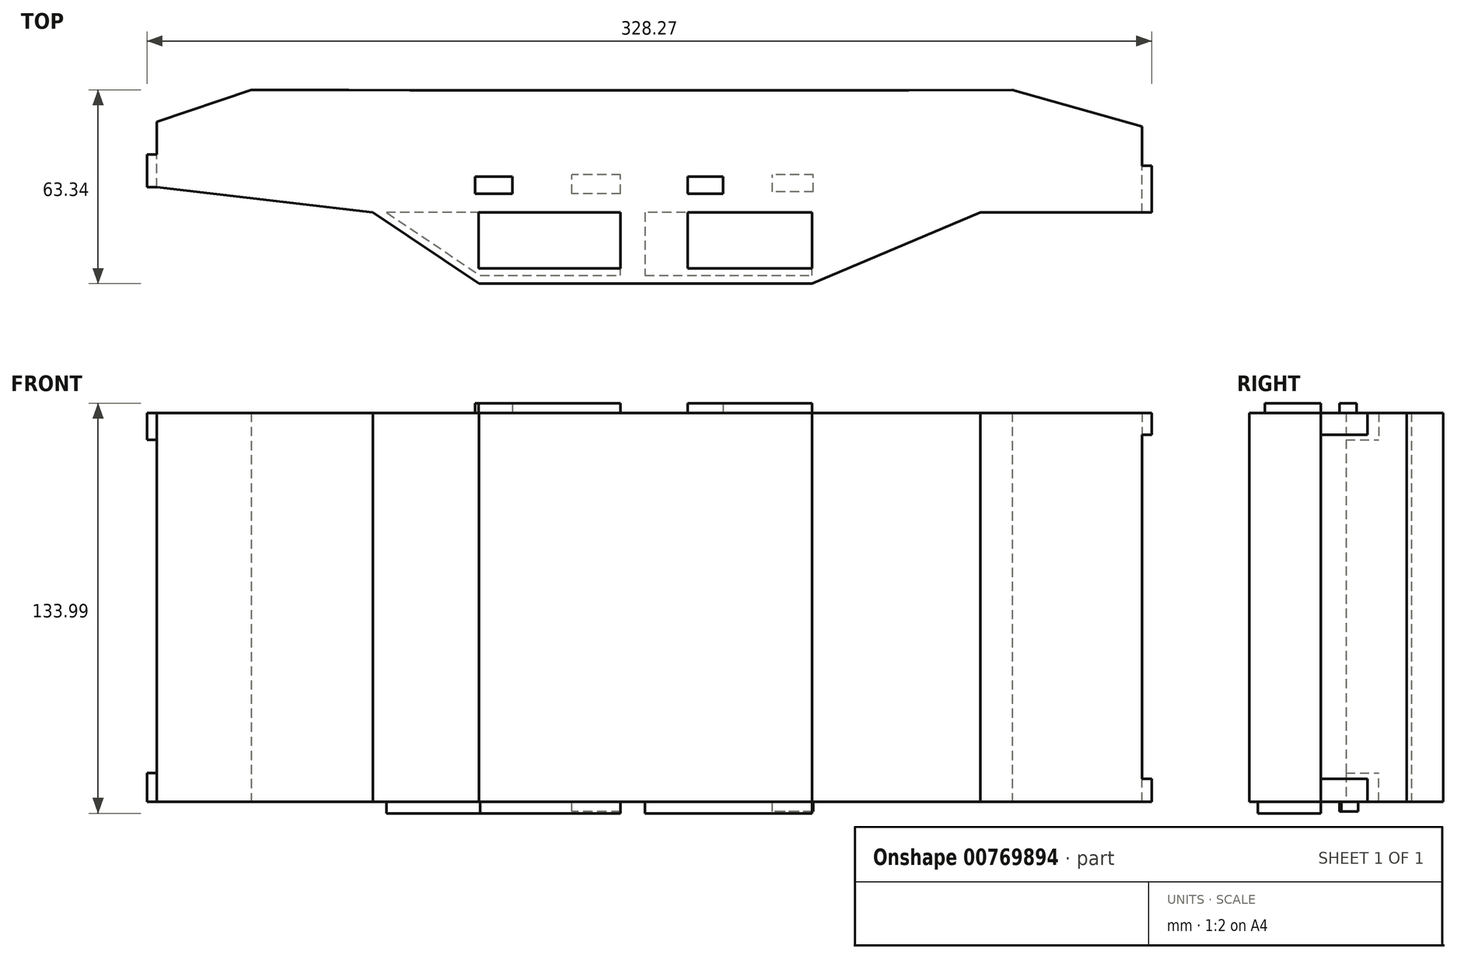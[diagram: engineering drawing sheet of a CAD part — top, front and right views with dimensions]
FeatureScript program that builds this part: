
annotation { "Feature Type Name" : "Feature", "Feature Type Description" : "" }
export const myFeature = defineFeature(function(context is Context, id is Id, definition is map)
    precondition{}
    {
        {
            var Q0;
            Q0=qCreatedBy(makeId("Top.planeOp"),FACE);
            var sketch = newSketch(context, id + "F0", { "sketchPlane" : qUnion([Q0])});
            skCircle(sketch, "E0", {"center": v(-68.64, 11.59) * mm, "radius": 18.95 * mm});
            skCircle(sketch, "E1", {"center": v(94.23, 11.59) * mm, "radius": 18.94 * mm});
            skLineSegment(sketch, "E2", {"start": v(-46.32, -70.57) * mm, "end": v(62.61, -70.57) * mm});
            skLineSegment(sketch, "E3", {"start": v(-46.32, -70.57) * mm, "end": v(-80.9, -47.31) * mm});
            skLineSegment(sketch, "E4", {"start": v(-80.9, -47.31) * mm, "end": v(-151.57, -39.05) * mm});
            skLineSegment(sketch, "E5", {"start": v(-151.57, -39.05) * mm, "end": v(-151.57, -17.64) * mm});
            skLineSegment(sketch, "E6", {"start": v(-151.57, -17.64) * mm, "end": v(-120.73, -7.23) * mm});
            skLineSegment(sketch, "E7", {"start": v(-120.73, -7.23) * mm, "end": v(-88.85, -7.23) * mm});
            skLineSegment(sketch, "E8", {"start": v(-46.32, -7.23) * mm, "end": v(62.61, -7.23) * mm});
            skLineSegment(sketch, "E9", {"start": v(62.61, -70.57) * mm, "end": v(117.59, -47.31) * mm});
            skLineSegment(sketch, "E10", {"start": v(117.59, -47.31) * mm, "end": v(170.34, -47.31) * mm});
            skLineSegment(sketch, "E11", {"start": v(170.34, -47.31) * mm, "end": v(170.34, -19.22) * mm});
            skLineSegment(sketch, "E12", {"start": v(170.34, -19.22) * mm, "end": v(127.98, -7.23) * mm});
            skLineSegment(sketch, "E13", {"start": v(-68.64, 11.59) * mm, "end": v(94.23, 11.59) * mm});
            skLineSegment(sketch, "E14", {"start": v(-68.64, -7.36) * mm, "end": v(94.23, -7.36) * mm});
            skLineSegment(sketch, "E15", {"start": v(-88.85, -7.23) * mm, "end": v(-68.64, -7.36) * mm});
            skLineSegment(sketch, "E16", {"start": v(127.98, -7.23) * mm, "end": v(94.23, -7.36) * mm});
            skSolve(sketch);
        }
        {
            var Q0;
            Q0=sQuery(id+"F0.wireOp",EDGE,"E0");
            var Q1;
            Q1=sQuery(id+"F0.wireOp",EDGE,"E1");
            extrude(context, id + "F1", {"bodyType" : ToolBodyType.SURFACE, "surfaceEntities" : qUnion([Q0, Q1]), "endBound" : BoundingType.SYMMETRIC, "depth" : 25.4 * mm, "offsetDistance" : 25.4 * mm});
        }
        {
            var Q0;
            Q0=qCreatedBy(makeId("Top.planeOp"),FACE);
            cPlane(context, id + "F2", {"entities" : qUnion([Q0]), "cplaneType" : CPlaneType.OFFSET, "offset" : 127 * mm, "width" : 152.4 * mm, "height" : 152.4 * mm});
        }
        {
            var Q0;
            Q0=qCreatedBy(id+"F2.planeOp",FACE);
            var sketch = newSketch(context, id + "F3", { "sketchPlane" : qUnion([Q0])});
            skCircle(sketch, "E17", {"center": v(-69.62, 11.2) * mm, "radius": 18.95 * mm});
            skCircle(sketch, "E18", {"center": v(95.63, 11.75) * mm, "radius": 18.95 * mm});
            skSolve(sketch);
        }
        {
            var Q0;
            Q0=sQuery(id+"F3.wireOp",EDGE,"E18");
            var Q1;
            Q1=sQuery(id+"F3.wireOp",EDGE,"E17");
            extrude(context, id + "F4", {"bodyType" : ToolBodyType.SURFACE, "surfaceEntities" : qUnion([Q0, Q1]), "endBound" : BoundingType.SYMMETRIC, "depth" : 25.4 * mm, "offsetDistance" : 25.4 * mm});
        }
        {
            var Q0;
            Q0=makeQuery(id+"F0.imprint","IMPRINT",FACE,{"disambiguationData":[TD([[makeQuery(id+"F0.imprint","IMPRINT",EDGE,{"derivedFrom":sQuery(id+"F0.wireOp",EDGE,"E2")}),1.0]])]});
            extrude(context, id + "F5", {"entities" : qUnion([Q0]), "depth" : 127 * mm, "offsetDistance" : 25.4 * mm});
        }
        {
            var Q0;
            Q0=makeQuery(id+"F5.opExtrude","CAP_FACE",FACE,{"disambiguationData":[OSD([sQuery(id+"F0.wireOp",EDGE,"E0"),sQuery(id+"F0.wireOp",EDGE,"E2"),sQuery(id+"F0.wireOp",EDGE,"E3"),sQuery(id+"F0.wireOp",EDGE,"E4"),sQuery(id+"F0.wireOp",EDGE,"E5"),sQuery(id+"F0.wireOp",EDGE,"E6"),sQuery(id+"F0.wireOp",EDGE,"E7"),sQuery(id+"F0.wireOp",EDGE,"E9"),sQuery(id+"F0.wireOp",EDGE,"E10"),sQuery(id+"F0.wireOp",EDGE,"E11"),sQuery(id+"F0.wireOp",EDGE,"E12"),sQuery(id+"F0.wireOp",EDGE,"E14"),sQuery(id+"F0.wireOp",EDGE,"E15"),sQuery(id+"F0.wireOp",EDGE,"E16")])],"isStart":true});
            var sketch = newSketch(context, id + "F6", { "sketchPlane" : qUnion([Q0])});
            skLineSegment(sketch, "E19", {"start": v(-76.42, 47.31) * mm, "end": v(-45.87, 67.86) * mm});
            skLineSegment(sketch, "E20", {"start": v(-45.87, 67.86) * mm, "end": v(0, 67.86) * mm});
            skLineSegment(sketch, "E21", {"start": v(0, 67.86) * mm, "end": v(0, 47.31) * mm});
            skLineSegment(sketch, "E22", {"start": v(0, 47.31) * mm, "end": v(-76.42, 47.31) * mm});
            skLineSegment(sketch, "E23", {"start": v(8.01, 67.86) * mm, "end": v(62.61, 67.86) * mm});
            skLineSegment(sketch, "E24", {"start": v(62.61, 67.86) * mm, "end": v(62.61, 47.31) * mm});
            skLineSegment(sketch, "E25", {"start": v(62.61, 47.31) * mm, "end": v(8.01, 47.31) * mm});
            skLineSegment(sketch, "E26", {"start": v(8.01, 47.31) * mm, "end": v(8.01, 67.86) * mm});
            skSolve(sketch);
        }
        {
            var Q0;
            Q0=makeQuery(id+"F6.imprint","IMPRINT",FACE,{"disambiguationData":[TD([[makeQuery(id+"F6.imprint","IMPRINT",EDGE,{"derivedFrom":sQuery(id+"F6.wireOp",EDGE,"E19")}),-1.0]])]});
            var Q1;
            Q1=makeQuery(id+"F6.imprint","IMPRINT",FACE,{"disambiguationData":[TD([[makeQuery(id+"F6.imprint","IMPRINT",EDGE,{"derivedFrom":sQuery(id+"F6.wireOp",EDGE,"E23")}),-1.0]])]});
            extrude(context, id + "F7", {"entities" : qUnion([Q0, Q1]), "operationType" : NewBodyOperationType.ADD, "depth" : 3.8 * mm, "offsetDistance" : 25.4 * mm});
        }
        {
            var Q0;
            Q0=makeQuery(id+"F5.opExtrude","SWEPT_FACE",FACE,{"disambiguationData":[OSD([sQuery(id+"F0.wireOp",EDGE,"E11")])]});
            var sketch = newSketch(context, id + "F8", { "sketchPlane" : qUnion([Q0])});
            skLineSegment(sketch, "E27.bottom", {"start": v(-47.31, 0) * mm, "end": v(-31.96, 0) * mm});
            skLineSegment(sketch, "E27.top", {"start": v(-47.31, 7.4) * mm, "end": v(-31.96, 7.4) * mm});
            skLineSegment(sketch, "E27.left", {"start": v(-47.31, 0) * mm, "end": v(-47.31, 7.4) * mm});
            skLineSegment(sketch, "E27.right", {"start": v(-31.96, 0) * mm, "end": v(-31.96, 7.4) * mm});
            skLineSegment(sketch, "E28.bottom", {"start": v(-47.31, 127) * mm, "end": v(-31.96, 127) * mm});
            skLineSegment(sketch, "E28.top", {"start": v(-47.31, 119.88) * mm, "end": v(-31.96, 119.88) * mm});
            skLineSegment(sketch, "E28.left", {"start": v(-47.31, 127) * mm, "end": v(-47.31, 119.88) * mm});
            skLineSegment(sketch, "E28.right", {"start": v(-31.96, 127) * mm, "end": v(-31.96, 119.88) * mm});
            skSolve(sketch);
        }
        {
            var Q0;
            Q0 = qSketchRegion(id + "F8", true);
            extrude(context, id + "F9", {"entities" : qUnion([Q0]), "operationType" : NewBodyOperationType.ADD, "depth" : 3.17 * mm, "offsetDistance" : 25.4 * mm});
        }
        {
            var Q0;
            Q0=makeQuery(id+"F5.opExtrude","SWEPT_FACE",FACE,{"disambiguationData":[OSD([sQuery(id+"F0.wireOp",EDGE,"E5")])]});
            var sketch = newSketch(context, id + "F10", { "sketchPlane" : qUnion([Q0])});
            skPoint(sketch, "E29.oppositeSnap0", {"position": v(28.35, 127) * mm});
            skLineSegment(sketch, "E29.bottom", {"start": v(39.05, 127) * mm, "end": v(28.35, 127) * mm});
            skLineSegment(sketch, "E29.top", {"start": v(39.05, 118.22) * mm, "end": v(28.35, 118.22) * mm});
            skLineSegment(sketch, "E29.left", {"start": v(39.05, 127) * mm, "end": v(39.05, 118.22) * mm});
            skLineSegment(sketch, "E29.right", {"start": v(28.35, 127) * mm, "end": v(28.35, 118.22) * mm});
            skLineSegment(sketch, "E30.bottom", {"start": v(39.05, 0) * mm, "end": v(28.35, 0) * mm});
            skLineSegment(sketch, "E30.top", {"start": v(39.05, 9.33) * mm, "end": v(28.35, 9.33) * mm});
            skLineSegment(sketch, "E30.left", {"start": v(39.05, 0) * mm, "end": v(39.05, 9.33) * mm});
            skLineSegment(sketch, "E30.right", {"start": v(28.35, 0) * mm, "end": v(28.35, 9.33) * mm});
            skSolve(sketch);
        }
        {
            var Q0;
            Q0=makeQuery(id+"F10.imprint","IMPRINT",FACE,{"disambiguationData":[TD([[makeQuery(id+"F10.imprint","IMPRINT",EDGE,{"derivedFrom":sQuery(id+"F10.wireOp",EDGE,"E29.bottom")}),1.0]])]});
            var Q1;
            Q1=makeQuery(id+"F10.imprint","IMPRINT",FACE,{"disambiguationData":[TD([[makeQuery(id+"F10.imprint","IMPRINT",EDGE,{"derivedFrom":sQuery(id+"F10.wireOp",EDGE,"E30.bottom")}),-1.0]])]});
            extrude(context, id + "F11", {"entities" : qUnion([Q0, Q1]), "operationType" : NewBodyOperationType.ADD, "depth" : 3.17 * mm, "offsetDistance" : 25.4 * mm});
        }
        {
            var Q0;
            Q0=makeQuery(id+"F11.boolean.opBoolean","MERGE",FACE,{"derivedFrom":[makeQuery(id+"F9.boolean.opBoolean","MERGE",FACE,{"derivedFrom":[makeQuery(id+"F5.opExtrude","CAP_FACE",FACE,{"disambiguationData":[OSD([sQuery(id+"F0.wireOp",EDGE,"E0"),sQuery(id+"F0.wireOp",EDGE,"E2"),sQuery(id+"F0.wireOp",EDGE,"E3"),sQuery(id+"F0.wireOp",EDGE,"E4"),sQuery(id+"F0.wireOp",EDGE,"E5"),sQuery(id+"F0.wireOp",EDGE,"E6"),sQuery(id+"F0.wireOp",EDGE,"E7"),sQuery(id+"F0.wireOp",EDGE,"E9"),sQuery(id+"F0.wireOp",EDGE,"E10"),sQuery(id+"F0.wireOp",EDGE,"E11"),sQuery(id+"F0.wireOp",EDGE,"E12"),sQuery(id+"F0.wireOp",EDGE,"E14"),sQuery(id+"F0.wireOp",EDGE,"E15"),sQuery(id+"F0.wireOp",EDGE,"E16")])],"isStart":false}),makeQuery(id+"F9.opExtrude","SWEPT_FACE",FACE,{"disambiguationData":[OSD([sQuery(id+"F8.wireOp",EDGE,"E28.bottom")])]})]}),makeQuery(id+"F11.opExtrude","SWEPT_FACE",FACE,{"disambiguationData":[OSD([sQuery(id+"F10.wireOp",EDGE,"E29.bottom")])]})]});
            var sketch = newSketch(context, id + "F12", { "sketchPlane" : qUnion([Q0])});
            skLineSegment(sketch, "E31", {"start": v(62.61, -65.57) * mm, "end": v(21.89, -65.57) * mm});
            skLineSegment(sketch, "E32", {"start": v(21.89, -65.57) * mm, "end": v(21.89, -47.31) * mm});
            skLineSegment(sketch, "E33", {"start": v(21.89, -47.31) * mm, "end": v(62.61, -47.31) * mm});
            skLineSegment(sketch, "E34", {"start": v(62.61, -47.31) * mm, "end": v(62.61, -65.57) * mm});
            skLineSegment(sketch, "E35", {"start": v(-46.45, -65.57) * mm, "end": v(-46.45, -47.31) * mm});
            skLineSegment(sketch, "E36", {"start": v(-46.45, -47.31) * mm, "end": v(0, -47.31) * mm});
            skLineSegment(sketch, "E37", {"start": v(0, -47.31) * mm, "end": v(0, -65.57) * mm});
            skLineSegment(sketch, "E38", {"start": v(0, -65.57) * mm, "end": v(-46.45, -65.57) * mm});
            skSolve(sketch);
        }
        {
            var Q0;
            Q0=makeQuery(id+"F12.imprint","IMPRINT",FACE,{"disambiguationData":[TD([[makeQuery(id+"F12.imprint","IMPRINT",EDGE,{"derivedFrom":sQuery(id+"F12.wireOp",EDGE,"E31")}),-1.0]])]});
            var Q1;
            Q1=makeQuery(id+"F12.imprint","IMPRINT",FACE,{"disambiguationData":[TD([[makeQuery(id+"F12.imprint","IMPRINT",EDGE,{"derivedFrom":sQuery(id+"F12.wireOp",EDGE,"E35")}),-1.0]])]});
            extrude(context, id + "F13", {"entities" : qUnion([Q0, Q1]), "operationType" : NewBodyOperationType.ADD, "depth" : 3.17 * mm, "offsetDistance" : 25.4 * mm});
        }
        {
            var Q0;
            Q0=makeQuery(id+"F11.boolean.opBoolean","MERGE",FACE,{"derivedFrom":[makeQuery(id+"F9.boolean.opBoolean","MERGE",FACE,{"derivedFrom":[makeQuery(id+"F5.opExtrude","CAP_FACE",FACE,{"disambiguationData":[OSD([sQuery(id+"F0.wireOp",EDGE,"E0"),sQuery(id+"F0.wireOp",EDGE,"E2"),sQuery(id+"F0.wireOp",EDGE,"E3"),sQuery(id+"F0.wireOp",EDGE,"E4"),sQuery(id+"F0.wireOp",EDGE,"E5"),sQuery(id+"F0.wireOp",EDGE,"E6"),sQuery(id+"F0.wireOp",EDGE,"E7"),sQuery(id+"F0.wireOp",EDGE,"E9"),sQuery(id+"F0.wireOp",EDGE,"E10"),sQuery(id+"F0.wireOp",EDGE,"E11"),sQuery(id+"F0.wireOp",EDGE,"E12"),sQuery(id+"F0.wireOp",EDGE,"E14"),sQuery(id+"F0.wireOp",EDGE,"E15"),sQuery(id+"F0.wireOp",EDGE,"E16")])],"isStart":true}),makeQuery(id+"F9.opExtrude","SWEPT_FACE",FACE,{"disambiguationData":[OSD([sQuery(id+"F8.wireOp",EDGE,"E27.bottom")])]})]}),makeQuery(id+"F11.opExtrude","SWEPT_FACE",FACE,{"disambiguationData":[OSD([sQuery(id+"F10.wireOp",EDGE,"E30.bottom")])]})]});
            var sketch = newSketch(context, id + "F14", { "sketchPlane" : qUnion([Q0])});
            skLineSegment(sketch, "E39.bottom", {"start": v(0, 41.12) * mm, "end": v(-15.9, 41.12) * mm});
            skLineSegment(sketch, "E39.top", {"start": v(0, 35) * mm, "end": v(-15.9, 35) * mm});
            skLineSegment(sketch, "E39.left", {"start": v(0, 41.12) * mm, "end": v(0, 35) * mm});
            skLineSegment(sketch, "E39.right", {"start": v(-15.9, 41.12) * mm, "end": v(-15.9, 35) * mm});
            skLineSegment(sketch, "E40.bottom", {"start": v(63, 40.57) * mm, "end": v(49.66, 40.57) * mm});
            skLineSegment(sketch, "E40.top", {"start": v(63, 35) * mm, "end": v(49.66, 35) * mm});
            skLineSegment(sketch, "E40.left", {"start": v(63, 40.57) * mm, "end": v(63, 35) * mm});
            skLineSegment(sketch, "E40.right", {"start": v(49.66, 40.57) * mm, "end": v(49.66, 35) * mm});
            skSolve(sketch);
        }
        {
            var Q0;
            Q0=makeQuery(id+"F14.imprint","IMPRINT",FACE,{"disambiguationData":[TD([[makeQuery(id+"F14.imprint","IMPRINT",EDGE,{"derivedFrom":sQuery(id+"F14.wireOp",EDGE,"E39.bottom")}),1.0]])]});
            var Q1;
            Q1=makeQuery(id+"F14.imprint","IMPRINT",FACE,{"disambiguationData":[TD([[makeQuery(id+"F14.imprint","IMPRINT",EDGE,{"derivedFrom":sQuery(id+"F14.wireOp",EDGE,"E40.bottom")}),1.0]])]});
            extrude(context, id + "F15", {"entities" : qUnion([Q0, Q1]), "operationType" : NewBodyOperationType.ADD, "depth" : 3.17 * mm, "offsetDistance" : 25.4 * mm});
        }
        {
            var Q0;
            Q0=makeQuery(id+"F11.boolean.opBoolean","MERGE",FACE,{"derivedFrom":[makeQuery(id+"F9.boolean.opBoolean","MERGE",FACE,{"derivedFrom":[makeQuery(id+"F5.opExtrude","CAP_FACE",FACE,{"disambiguationData":[OSD([sQuery(id+"F0.wireOp",EDGE,"E0"),sQuery(id+"F0.wireOp",EDGE,"E2"),sQuery(id+"F0.wireOp",EDGE,"E3"),sQuery(id+"F0.wireOp",EDGE,"E4"),sQuery(id+"F0.wireOp",EDGE,"E5"),sQuery(id+"F0.wireOp",EDGE,"E6"),sQuery(id+"F0.wireOp",EDGE,"E7"),sQuery(id+"F0.wireOp",EDGE,"E9"),sQuery(id+"F0.wireOp",EDGE,"E10"),sQuery(id+"F0.wireOp",EDGE,"E11"),sQuery(id+"F0.wireOp",EDGE,"E12"),sQuery(id+"F0.wireOp",EDGE,"E14"),sQuery(id+"F0.wireOp",EDGE,"E15"),sQuery(id+"F0.wireOp",EDGE,"E16")])],"isStart":false}),makeQuery(id+"F9.opExtrude","SWEPT_FACE",FACE,{"disambiguationData":[OSD([sQuery(id+"F8.wireOp",EDGE,"E28.bottom")])]})]}),makeQuery(id+"F11.opExtrude","SWEPT_FACE",FACE,{"disambiguationData":[OSD([sQuery(id+"F10.wireOp",EDGE,"E29.bottom")])]})]});
            var sketch = newSketch(context, id + "F16", { "sketchPlane" : qUnion([Q0])});
            skLineSegment(sketch, "E41.bottom", {"start": v(-47.56, -41.12) * mm, "end": v(-35.34, -41.12) * mm});
            skLineSegment(sketch, "E41.top", {"start": v(-47.56, -35.57) * mm, "end": v(-35.34, -35.57) * mm});
            skLineSegment(sketch, "E41.left", {"start": v(-47.56, -41.12) * mm, "end": v(-47.56, -35.57) * mm});
            skLineSegment(sketch, "E41.right", {"start": v(-35.34, -41.12) * mm, "end": v(-35.34, -35.57) * mm});
            skLineSegment(sketch, "E42.bottom", {"start": v(21.89, -41.12) * mm, "end": v(33.55, -41.12) * mm});
            skLineSegment(sketch, "E42.top", {"start": v(21.89, -35.57) * mm, "end": v(33.55, -35.57) * mm});
            skLineSegment(sketch, "E42.left", {"start": v(21.89, -41.12) * mm, "end": v(21.89, -35.57) * mm});
            skLineSegment(sketch, "E42.right", {"start": v(33.55, -41.12) * mm, "end": v(33.55, -35.57) * mm});
            skSolve(sketch);
        }
        {
            var Q0;
            Q0=makeQuery(id+"F16.imprint","IMPRINT",FACE,{"disambiguationData":[TD([[makeQuery(id+"F16.imprint","IMPRINT",EDGE,{"derivedFrom":sQuery(id+"F16.wireOp",EDGE,"E42.bottom")}),1.0]])]});
            var Q1;
            Q1=makeQuery(id+"F16.imprint","IMPRINT",FACE,{"disambiguationData":[TD([[makeQuery(id+"F16.imprint","IMPRINT",EDGE,{"derivedFrom":sQuery(id+"F16.wireOp",EDGE,"E41.bottom")}),1.0]])]});
            extrude(context, id + "F17", {"entities" : qUnion([Q0, Q1]), "operationType" : NewBodyOperationType.ADD, "depth" : 3.17 * mm, "offsetDistance" : 25.4 * mm});
        }
    });
